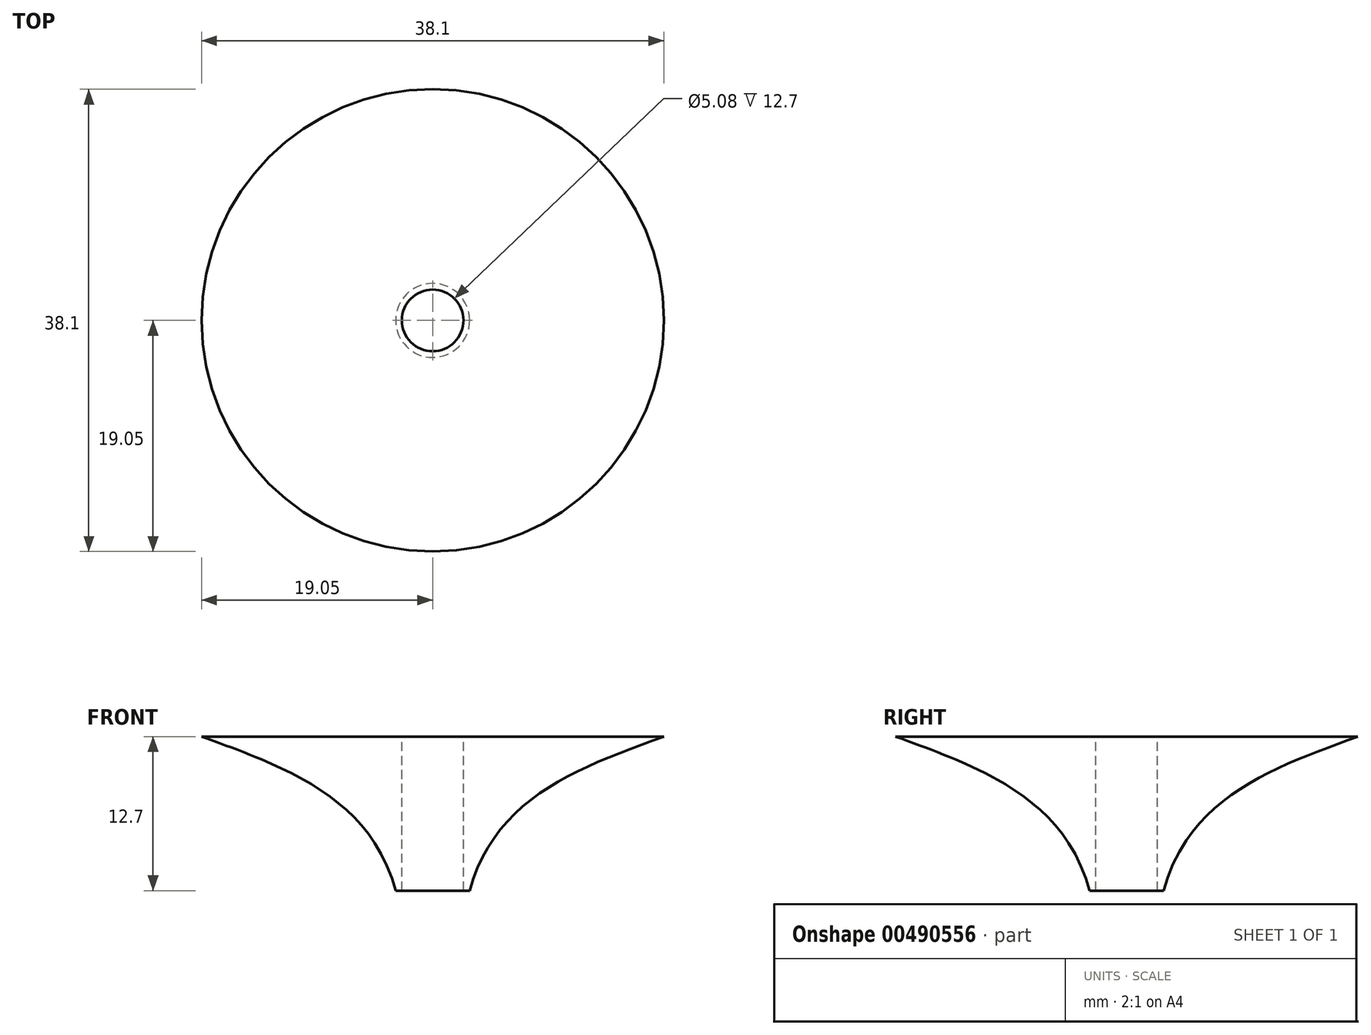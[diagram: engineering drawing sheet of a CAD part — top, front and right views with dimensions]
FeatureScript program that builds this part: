
annotation { "Feature Type Name" : "Feature", "Feature Type Description" : "" }
export const myFeature = defineFeature(function(context is Context, id is Id, definition is map)
    precondition{}
    {
        {
            var Q0;
            Q0=qCreatedBy(makeId("Front.planeOp"),FACE);
            var sketch = newSketch(context, id + "F0", { "sketchPlane" : qUnion([Q0])});
            skLineSegment(sketch, "E0.bottom", {"start": v(0, 0) * mm, "end": v(-19.05, 0) * mm});
            skLineSegment(sketch, "E0.left", {"start": v(0, 0) * mm, "end": v(0, -12.7) * mm, "construction": true});
            skFitSpline(sketch, "E1", {"points": [v(-19.05, 0) * mm, v(-3.05, -12.7) * mm], "startDerivative": vector(21.3, -7.77) * mm, "endDerivative": vector(6.33, -23.03) * mm});
            skLineSegment(sketch, "E2", {"start": v(-3.05, -12.7) * mm, "end": v(0, -12.7) * mm});
            skLineSegment(sketch, "E3.MirrorCS", {"start": v(0, 0) * mm, "end": v(19.05, 0) * mm});
            skFitSpline(sketch, "E4.MirrorCS", {"points": [v(19.05, 0) * mm, v(3.05, -12.7) * mm], "startDerivative": vector(-21.3, -7.77) * mm, "endDerivative": vector(-6.33, -23.03) * mm});
            skLineSegment(sketch, "E5.MirrorCS", {"start": v(3.05, -12.7) * mm, "end": v(0, -12.7) * mm});
            skPoint(sketch, "E6.oppositeSnap0", {"position": v(0, -6.35) * mm});
            skLineSegment(sketch, "E6.bottom", {"start": v(-19.05, 0) * mm, "end": v(0, 0) * mm});
            skLineSegment(sketch, "E6.top", {"start": v(-19.05, 38.1) * mm, "end": v(0, 38.1) * mm, "construction": true});
            skLineSegment(sketch, "E6.left", {"start": v(-19.05, 0) * mm, "end": v(-19.05, 38.1) * mm, "construction": true});
            skLineSegment(sketch, "E6.right", {"start": v(0, 0) * mm, "end": v(0, 38.1) * mm});
            skFitSpline(sketch, "E7", {"points": [v(-19.05, 0) * mm, v(0, 38.1) * mm], "startDerivative": vector(51.44, 7.7) * mm, "endDerivative": vector(6.28, 67.55) * mm});
            skFitSpline(sketch, "E8.MirrorCS", {"points": [v(19.05, 0) * mm, v(0, 38.1) * mm], "startDerivative": vector(-51.44, 7.7) * mm, "endDerivative": vector(-6.28, 67.55) * mm});
            skLineSegment(sketch, "E9.bottom", {"start": v(-19.05, 0) * mm, "end": v(0, 0) * mm, "construction": true});
            skLineSegment(sketch, "E9.top", {"start": v(-19.05, -12.7) * mm, "end": v(0, -12.7) * mm, "construction": true});
            skLineSegment(sketch, "E9.left", {"start": v(-19.05, 0) * mm, "end": v(-19.05, -12.7) * mm, "construction": true});
            skLineSegment(sketch, "E9.right", {"start": v(0, 0) * mm, "end": v(0, -12.7) * mm});
            skSolve(sketch);
        }
        {
            var Q0;
            Q0=makeQuery(id+"F0.imprint","IMPRINT",FACE,{"disambiguationData":[TD([[makeQuery(id+"F0.imprint","IMPRINT",EDGE,{"derivedFrom":sQuery(id+"F0.wireOp",EDGE,"E1")}),1.0]])]});
            var Q1;
            Q1=makeQuery(id+"F0.imprint","IMPRINT",FACE,{"disambiguationData":[TD([[makeQuery(id+"F0.imprint","IMPRINT",EDGE,{"derivedFrom":sQuery(id+"F0.wireOp",EDGE,"E6.bottom")}),1.0]])]});
            var Q2;
            Q2=sQuery(id+"F0.wireOp",EDGE,"E9.right");
            revolve(context, id + "F1", {"entities" : qUnion([Q0, Q1]), "axis" : qUnion([Q2]), "revolveType" : RevolveType.FULL});
        }
        {
            var Q0;
            Q0=qCreatedBy(makeId("Top.planeOp"),FACE);
            var sketch = newSketch(context, id + "F2", { "sketchPlane" : qUnion([Q0])});
            skCircle(sketch, "E10", {"center": v(0, 0) * mm, "radius": 2.54 * mm});
            skLineSegment(sketch, "E11", {"start": v(0, 0) * mm, "end": v(-2.54, 0) * mm});
            skSolve(sketch);
        }
        {
            var Q0;
            Q0 = qSketchRegion(id + "F2", true);
            var Q1;
            Q1=sQuery(id+"F2.wireOp",EDGE,"E10");
            extrude(context, id + "F3", {"entities" : qUnion([Q0]), "operationType" : NewBodyOperationType.REMOVE, "surfaceEntities" : qUnion([Q1]), "oppositeDirection" : true, "depth" : 25.4 * mm});
        }
    });
